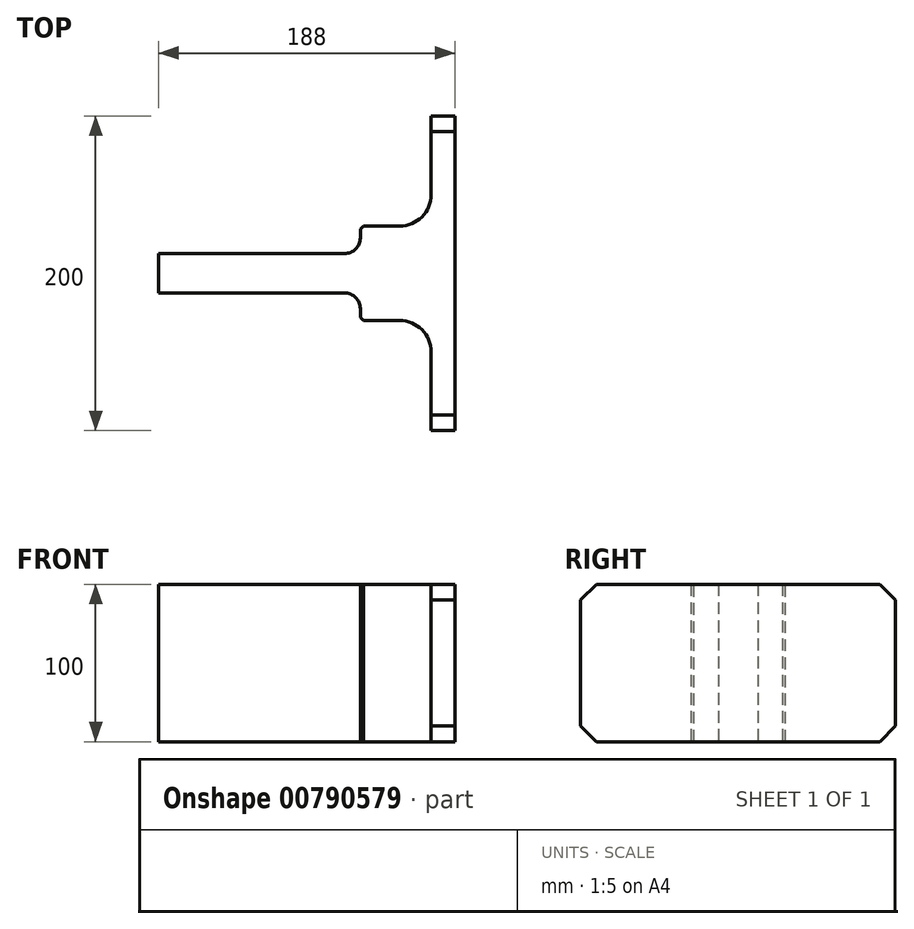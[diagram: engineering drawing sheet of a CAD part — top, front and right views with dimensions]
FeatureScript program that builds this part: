
annotation { "Feature Type Name" : "Feature", "Feature Type Description" : "" }
export const myFeature = defineFeature(function(context is Context, id is Id, definition is map)
    precondition{}
    {
        {
            var Q0;
            Q0=qCreatedBy(makeId("Top.planeOp"),FACE);
            var sketch = newSketch(context, id + "F0", { "sketchPlane" : qUnion([Q0])});
            skLineSegment(sketch, "E0", {"start": v(0, 0) * mm, "end": v(0, 200) * mm});
            skLineSegment(sketch, "E1", {"start": v(0, 200) * mm, "end": v(-15, 200) * mm});
            skLineSegment(sketch, "E2", {"start": v(-15, 200) * mm, "end": v(-15, 130) * mm});
            skLineSegment(sketch, "E3", {"start": v(-15, 130) * mm, "end": v(-60, 130) * mm});
            skLineSegment(sketch, "E4", {"start": v(-60, 130) * mm, "end": v(-60, 112.5) * mm});
            skLineSegment(sketch, "E5", {"start": v(-60, 112.5) * mm, "end": v(-188, 112.5) * mm});
            skLineSegment(sketch, "E6", {"start": v(-188, 112.5) * mm, "end": v(-188, 87.5) * mm});
            skLineSegment(sketch, "E7", {"start": v(-188, 87.5) * mm, "end": v(-60, 87.5) * mm});
            skLineSegment(sketch, "E8", {"start": v(-60, 87.5) * mm, "end": v(-60, 70) * mm});
            skLineSegment(sketch, "E9", {"start": v(-60, 70) * mm, "end": v(-15, 70) * mm});
            skLineSegment(sketch, "E10", {"start": v(-15, 70) * mm, "end": v(-15, 0) * mm});
            skLineSegment(sketch, "E11", {"start": v(-15, 0) * mm, "end": v(0, 0) * mm});
            skSolve(sketch);
        }
        {
            var Q0;
            Q0=makeQuery(id+"F0.imprint","IMPRINT",FACE,{"disambiguationData":[TD([[makeQuery(id+"F0.imprint","IMPRINT",EDGE,{"derivedFrom":sQuery(id+"F0.wireOp",EDGE,"E0")}),1.0]])]});
            extrude(context, id + "F1", {"entities" : qUnion([Q0]), "depth" : 100 * mm, "offsetDistance" : 25 * mm});
        }
        {
            var Q0;
            Q0=makeQuery(id+"F1.opExtrude","SWEPT_EDGE",EDGE,{"disambiguationData":[OSD([sQuery(id+"F0.wireOp",EDGE,"E9"),sQuery(id+"F0.wireOp",EDGE,"E10")])]});
            var Q1;
            Q1=makeQuery(id+"F1.opExtrude","SWEPT_EDGE",EDGE,{"disambiguationData":[OSD([sQuery(id+"F0.wireOp",EDGE,"E2"),sQuery(id+"F0.wireOp",EDGE,"E3")])]});
            fillet(context, id + "F2", {"entities" : qUnion([Q0, Q1]), "radius" : 20 * mm, "tangentPropagation" : true, "allowEdgeOverflow" : false});
        }
        {
            var Q0;
            Q0=makeQuery(id+"F1.opExtrude","SWEPT_EDGE",EDGE,{"disambiguationData":[OSD([sQuery(id+"F0.wireOp",EDGE,"E7"),sQuery(id+"F0.wireOp",EDGE,"E8")])]});
            var Q1;
            Q1=makeQuery(id+"F1.opExtrude","SWEPT_EDGE",EDGE,{"disambiguationData":[OSD([sQuery(id+"F0.wireOp",EDGE,"E4"),sQuery(id+"F0.wireOp",EDGE,"E5")])]});
            fillet(context, id + "F3", {"entities" : qUnion([Q0, Q1]), "radius" : 10 * mm, "tangentPropagation" : true, "allowEdgeOverflow" : false});
        }
        {
            var Q0;
            Q0=makeQuery(id+"F1.opExtrude","CAP_EDGE",EDGE,{"disambiguationData":[OSD([sQuery(id+"F0.wireOp",EDGE,"E1")])],"isStart":false});
            var Q1;
            Q1=makeQuery(id+"F1.opExtrude","CAP_EDGE",EDGE,{"disambiguationData":[OSD([sQuery(id+"F0.wireOp",EDGE,"E11")])],"isStart":false});
            var Q2;
            Q2=makeQuery(id+"F1.opExtrude","CAP_EDGE",EDGE,{"disambiguationData":[OSD([sQuery(id+"F0.wireOp",EDGE,"E11")])],"isStart":true});
            var Q3;
            Q3=makeQuery(id+"F1.opExtrude","CAP_EDGE",EDGE,{"disambiguationData":[OSD([sQuery(id+"F0.wireOp",EDGE,"E1")])],"isStart":true});
            chamfer(context, id + "F4", {"entities" : qUnion([Q0, Q1, Q2, Q3]), "width" : 10 * mm, "tangentPropagation" : true});
        }
        {
            var Q0;
            Q0=makeQuery(id+"F1.opExtrude","SWEPT_EDGE",EDGE,{"disambiguationData":[OSD([sQuery(id+"F0.wireOp",EDGE,"E8"),sQuery(id+"F0.wireOp",EDGE,"E9")])]});
            var Q1;
            Q1=makeQuery(id+"F1.opExtrude","SWEPT_EDGE",EDGE,{"disambiguationData":[OSD([sQuery(id+"F0.wireOp",EDGE,"E3"),sQuery(id+"F0.wireOp",EDGE,"E4")])]});
            chamfer(context, id + "F5", {"entities" : qUnion([Q0, Q1]), "width" : 2 * mm, "tangentPropagation" : true});
        }
    });
